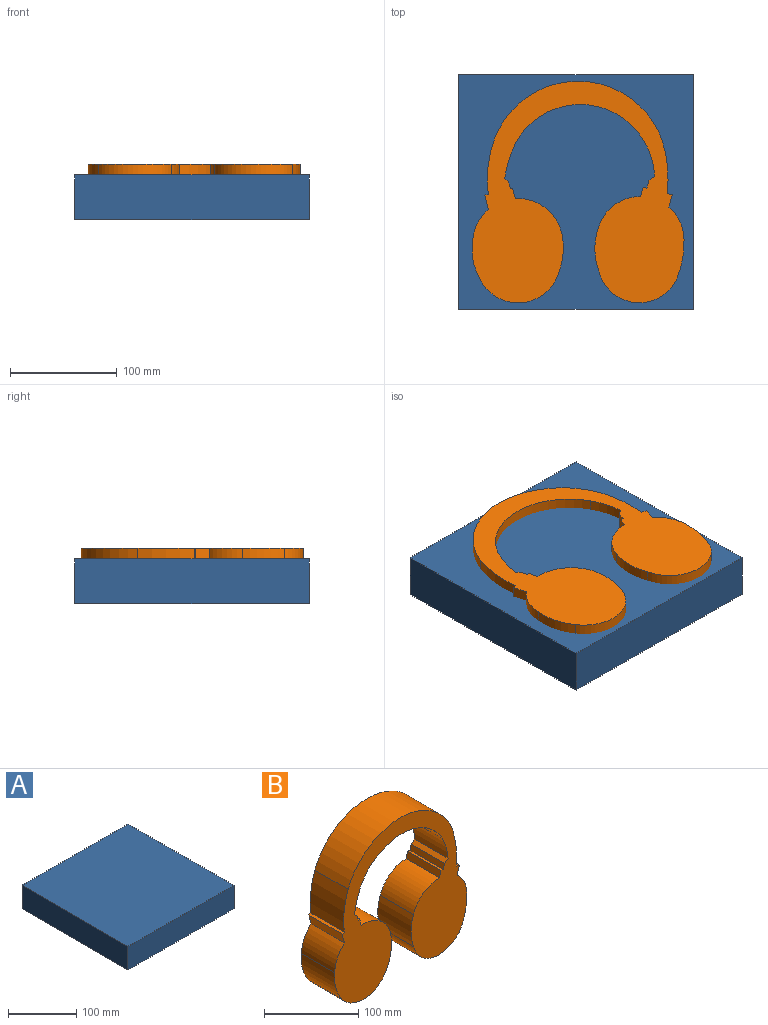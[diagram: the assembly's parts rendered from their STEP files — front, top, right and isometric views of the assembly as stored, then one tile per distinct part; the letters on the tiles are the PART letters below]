
ASSEMBLY  parts=2 mates=1
PART A: 6 faces, bbox 220x220x42 mm
  f0: plane 220x42mm, normal (0,-1,0), area 9240mm2, adj f1,f3,f4,f5
  f1: plane 220x42mm, normal (1,0,0), area 9240mm2, adj f0,f2,f4,f5
  f2: plane 220x42mm, normal (0,1,0), area 9240mm2, adj f1,f3,f4,f5
  f3: plane 220x42mm, normal (-1,0,0), area 9240mm2, adj f0,f2,f4,f5
  f4: plane 220x220mm, normal (0,0,1), area 48400mm2, adj f0,f1,f2,f3
  f5: plane 220x220mm, normal (0,0,-1), area 48400mm2, adj f0,f1,f2,f3
PART B: 30 faces, bbox 198.5x50x208.4 mm
  f0: plane 50x9.72mm, normal (0.97,0,0.25), area 502.5mm2, adj f1,f27,f28,f29
  f1: plane 50x2.18mm, normal (-0.25,0,0.97), area 112.8mm2, adj f0,f2,f28,f29
  f2: plane 50x6.49mm, normal (0.97,0,0.25), area 335.2mm2, adj f1,f3,f28,f29
  f3: plane 50x3.71mm, normal (0.65,0,0.76), area 245.5mm2, adj f2,f4,f28,f29
  f4: cylinder r=120.14mm len=50mm, axis (0,1,0), area 1826.6mm2, adj f3,f5,f28,f29
  f5: cylinder r=69.23mm len=120.97mm, axis (0,1,0), area 7358.3mm2, adj f4,f6,f28,f29
  f6: cylinder r=68.7mm len=50mm, axis (0,1,0), area 1597.8mm2, adj f5,f7,f28,f29
  f7: plane 50x5.32mm, normal (-0.62,0,0.78), area 339.2mm2, adj f6,f8,f28,f29
  f8: plane 50x7.11mm, normal (-0.97,0,0.25), area 366.6mm2, adj f7,f9,f28,f29
  f9: plane 50x3.62mm, normal (0.25,0,0.97), area 186.5mm2, adj f8,f10,f28,f29
  f10: plane 50x8.74mm, normal (-0.97,0,0.25), area 450.6mm2, adj f9,f11,f28,f29
  f11: cylinder r=41mm len=50mm, axis (0,1,0), area 2570.1mm2, adj f10,f12,f28,f29
  f12: cylinder r=60.37mm len=50mm, axis (0,1,0), area 2131.6mm2, adj f11,f13,f28,f29
  f13: cylinder r=38.99mm len=73.2mm, axis (0,1,0), area 4801.8mm2, adj f12,f14,f28,f29
  f14: cylinder r=90.81mm len=50mm, axis (0,1,0), area 1885.5mm2, adj f13,f15,f28,f29
  f15: cylinder r=41mm len=50mm, axis (0,1,0), area 1745.6mm2, adj f14,f16,f28,f29
  f16: plane 50x11.38mm, normal (0.96,0,-0.28), area 593.5mm2, adj f15,f17,f28,f29
  f17: plane 50x4.94mm, normal (0.25,0,0.97), area 254.8mm2, adj f16,f18,f28,f29
  f18: cylinder r=123.89mm len=50mm, axis (0,1,0), area 2499.4mm2, adj f17,f19,f28,f29
  f19: cylinder r=83.79mm len=157.01mm, axis (0,1,0), area 10170.5mm2, adj f18,f20,f28,f29
  f20: cylinder r=110.78mm len=52.84mm, axis (0,1,0), area 2683.9mm2, adj f19,f21,f28,f29
  f21: plane 50x3.25mm, normal (-0.25,0,0.97), area 167.8mm2, adj f20,f22,f28,f29
  f22: plane 50x13.3mm, normal (-0.97,0,-0.25), area 687.1mm2, adj f21,f23,f28,f29
  f23: cylinder r=42.43mm len=50mm, axis (0,1,0), area 1779mm2, adj f22,f24,f28,f29
  f24: cylinder r=56.62mm len=50mm, axis (0,1,0), area 2042.1mm2, adj f23,f25,f28,f29
  f25: cylinder r=39.6mm len=67.78mm, axis (0,1,0), area 4075.6mm2, adj f24,f26,f28,f29
  f26: cylinder r=67.04mm len=50mm, axis (0,1,0), area 1886.4mm2, adj f25,f27,f28,f29
  f27: cylinder r=42.43mm len=50mm, axis (0,1,0), area 3371.9mm2, adj f0,f26,f28,f29
  f28: plane 208.37x198.54mm, normal (0,-1,0), area 19072.7mm2, adj f0,f1,f2,f3,f4,f5,f6,f7
  f29: plane 208.37x198.54mm, normal (0,1,0), area 19072.7mm2, adj f0,f1,f2,f3,f4,f5,f6,f7
PLACE A t=(-0.21,-0.11,-20.99)mm fixed
PLACE B rot(axis=(-1,0,0),90deg) t=(3.37,-0.47,-18.99)mm
MATE planar A.f5 <-> B.f13  axis (0,0,-1) through (-0.21,-0.11,-20.99)mm
